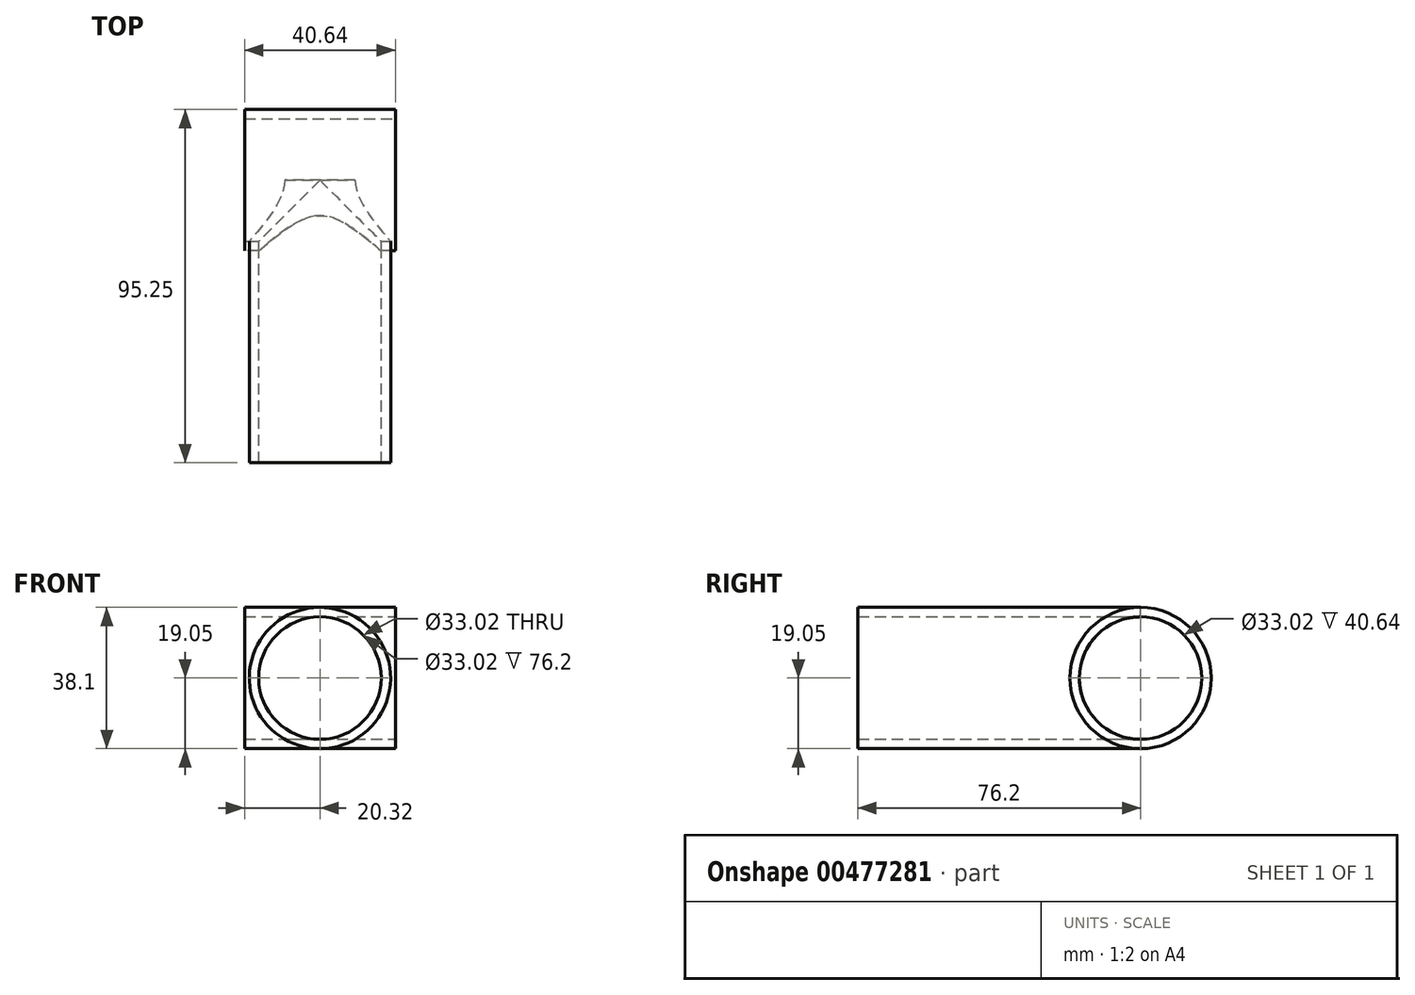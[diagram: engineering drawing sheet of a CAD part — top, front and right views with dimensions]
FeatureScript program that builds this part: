
annotation { "Feature Type Name" : "Feature", "Feature Type Description" : "" }
export const myFeature = defineFeature(function(context is Context, id is Id, definition is map)
    precondition{}
    {
        {
            var Q0;
            Q0=qCreatedBy(makeId("Front.planeOp"),FACE);
            var sketch = newSketch(context, id + "F0", { "sketchPlane" : qUnion([Q0])});
            skCircle(sketch, "E0", {"center": v(0, 0) * mm, "radius": 19.05 * mm});
            skSolve(sketch);
        }
        {
            var Q0;
            Q0=makeQuery(id+"F0.imprint","IMPRINT",FACE,{"disambiguationData":[TD([[makeQuery(id+"F0.imprint","IMPRINT",EDGE,{"derivedFrom":sQuery(id+"F0.wireOp",EDGE,"E0")}),1.0]])]});
            extrude(context, id + "F1", {"entities" : qUnion([Q0]), "depth" : 76.2 * mm});
        }
        {
            var Q0;
            Q0=qCreatedBy(makeId("Right.planeOp"),FACE);
            var sketch = newSketch(context, id + "F2", { "sketchPlane" : qUnion([Q0])});
            skCircle(sketch, "E1", {"center": v(0, 0) * mm, "radius": 19.05 * mm});
            skSolve(sketch);
        }
        {
            var Q0;
            Q0=makeQuery(id+"F2.imprint","IMPRINT",FACE,{"disambiguationData":[TD([[makeQuery(id+"F2.imprint","IMPRINT",EDGE,{"derivedFrom":sQuery(id+"F2.wireOp",EDGE,"E1")}),1.0]])]});
            extrude(context, id + "F3", {"entities" : qUnion([Q0]), "endBound" : BoundingType.SYMMETRIC, "depth" : 40.64 * mm});
        }
        {
            var Q0;
            Q0=sQuery(id+"F2.wireOp",VERTEX,"E1.center");
            var Q1;
            Q1=makeQuery(id+"F1.opExtrude","SWEPT_BODY",BODY,{"disambiguationData":[OSD([sQuery(id+"F0.wireOp",EDGE,"E0")])]});
            var Q2;
            Q2=makeQuery(id+"F3.opExtrude","SWEPT_BODY",BODY,{"disambiguationData":[OSD([sQuery(id+"F2.wireOp",EDGE,"E1")])]});
            hole(context, id + "F4", {"style" : HoleStyle.SIMPLE, "endStyle" : HoleEndStyle.THROUGH, "holeDiameter" : 33.02 * mm, "isTappedThrough" : true, "tappedDepth" : 12.7 * mm, "tapClearance" : 3, "startFromSketch" : true, "locations" : qUnion([Q0]), "scope" : qUnion([Q1, Q2])});
        }
        {
            var Q0;
            Q0=sQuery(id+"F2.wireOp",VERTEX,"E1.center");
            var Q1;
            Q1=makeQuery(id+"F1.opExtrude","SWEPT_BODY",BODY,{"disambiguationData":[OSD([sQuery(id+"F0.wireOp",EDGE,"E0")])]});
            var Q2;
            Q2=makeQuery(id+"F3.opExtrude","SWEPT_BODY",BODY,{"disambiguationData":[OSD([sQuery(id+"F2.wireOp",EDGE,"E1")])]});
            hole(context, id + "F5", {"style" : HoleStyle.SIMPLE, "endStyle" : HoleEndStyle.THROUGH, "oppositeDirection" : true, "holeDiameter" : 33.02 * mm, "isTappedThrough" : true, "tappedDepth" : 12.7 * mm, "tapClearance" : 3, "startFromSketch" : true, "locations" : qUnion([Q0]), "scope" : qUnion([Q1, Q2])});
        }
        {
            var Q0;
            Q0=sQuery(id+"F0.wireOp",VERTEX,"E0.center");
            var Q1;
            Q1=makeQuery(id+"F1.opExtrude","SWEPT_BODY",BODY,{"disambiguationData":[OSD([sQuery(id+"F0.wireOp",EDGE,"E0")])]});
            var Q2;
            Q2=makeQuery(id+"F3.opExtrude","SWEPT_BODY",BODY,{"disambiguationData":[OSD([sQuery(id+"F2.wireOp",EDGE,"E1")])]});
            hole(context, id + "F6", {"style" : HoleStyle.SIMPLE, "endStyle" : HoleEndStyle.BLIND, "oppositeDirection" : true, "holeDiameter" : 33.02 * mm, "holeDepth" : 63.5 * mm, "isTappedThrough" : true, "tappedDepth" : 12.7 * mm, "tapClearance" : 3, "locations" : qUnion([Q0]), "scope" : qUnion([Q1, Q2])});
        }
    });
